# Revit family: Furniture_Table_593 MT
name_source: partatom
category: Furniture
units: mm (PartAtom-declared; Revit-internal decimal feet)

## family parameters
Always vertical = No
Cut with Voids When Loaded = No
OmniClass Number = 23.21.23.15.17
Room Calculation Point = No
Shared = No
Work Plane-Based = Yes

## types (5) — shared parameters
BIMobject category = Table
BIMobject category code = furniture-table
BIMobject main category = Furniture
BIMobject main category code = furniture
Brand url = https://www.sandlerseating.com
Description = Table
Design country = Brasil
Edition number = 1
Frame Material = Steel - Paint Finish - Black
IFC Classification = Furnishing Element
Manufacturer = Sandler
Manufacturer country = USA
Manufacturer name = Sandler
Masterformat 2014 Code = 12 48 43.13
Masterformat 2014 Description = Table Mats
OmniClass Code = 23-21 23 15 17
Product Guid = ??
Product SKU = ??
Product data url = https://www.sandlerseating.com
Product family = Furniture
Product group = Table
Product url = https://www.sandlerseating.com
QR code = https://www.sandlerseating.com
Top Material = Wood - Cherry
Uniformat II Description = Movable Furnishings
zero-valued in all types: Default Elevation

## per-type parameters (varying)
| type | Type Top |
| 593 MT - ROUND TOP 44" | TP01 - 593 - Round 110 |
| 593 MT - ROUND TOP 48" | TP01 - 593 - Round 120 |
| 593 MT - ROUND TOP 52" | TP01 - 593 - Round 130 |
| 593 MT - SQUARE TOP 44" | TP01 - 593 - Square 110 |
| 593 MT - SQUARE TOP 40" | TP01 - 593 - Square 100 |

note: column(s) folded — value = type name in every type: Model, Product name

## geometry (parser evidence)
native form markers: Blend x4, Sweep x11
no freeform markers — native parametric forms only
